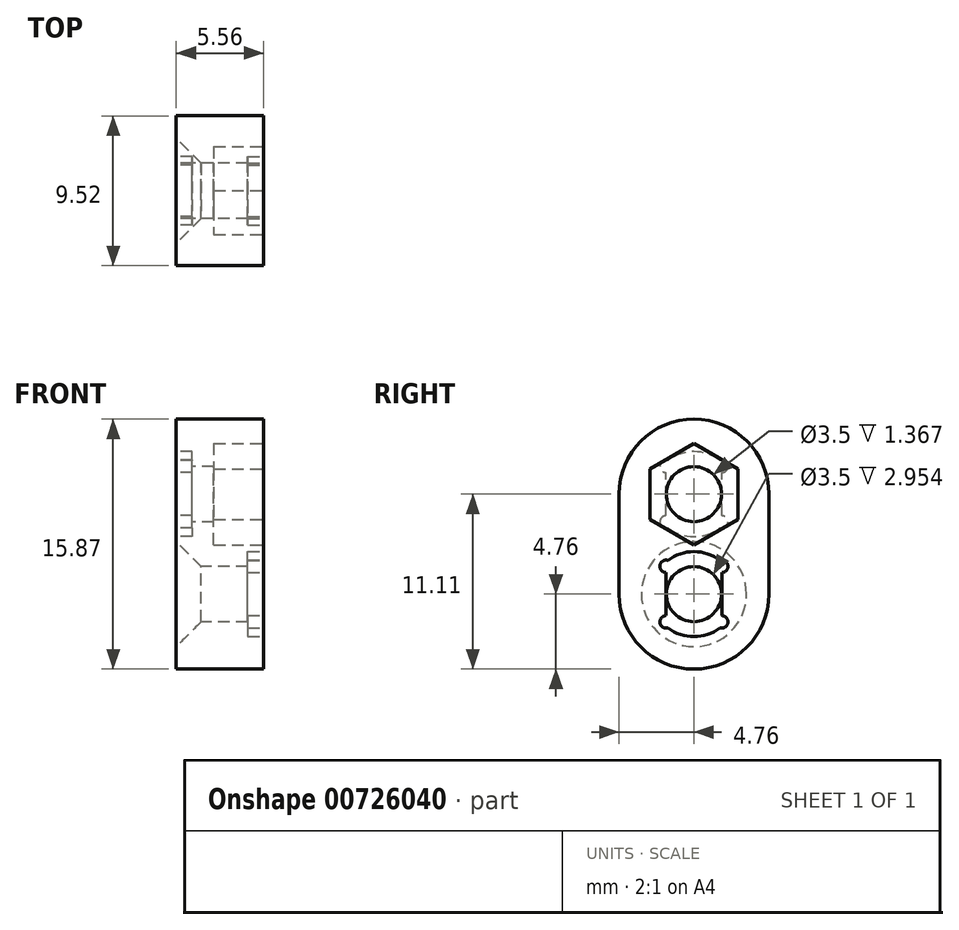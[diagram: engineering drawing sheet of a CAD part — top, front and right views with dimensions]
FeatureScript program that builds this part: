
annotation { "Feature Type Name" : "Feature", "Feature Type Description" : "" }
export const myFeature = defineFeature(function(context is Context, id is Id, definition is map)
    precondition{}
    {
        {
            var Q0;
            Q0=qCreatedBy(makeId("Right.planeOp"),FACE);
            var sketch = newSketch(context, id + "F0", { "sketchPlane" : qUnion([Q0])});
            skCircle(sketch, "E0", {"center": v(0, 0) * mm, "radius": 4.76 * mm});
            skCircle(sketch, "E1", {"center": v(0, 0) * mm, "radius": 1.75 * mm});
            skCircle(sketch, "E2", {"center": v(0, -6.35) * mm, "radius": 4.76 * mm});
            skCircle(sketch, "E3", {"center": v(0, -6.35) * mm, "radius": 1.75 * mm});
            skLineSegment(sketch, "E4", {"start": v(-4.76, 0) * mm, "end": v(-4.76, -6.35) * mm});
            skLineSegment(sketch, "E5", {"start": v(4.76, 0) * mm, "end": v(4.76, -6.35) * mm});
            skSolve(sketch);
        }
        {
            var Q0;
            Q0=makeQuery(id+"F0.imprint","IMPRINT",FACE,{"disambiguationData":[TD([[makeQuery(id+"F0.imprint","IMPRINT",EDGE,{"derivedFrom":sQuery(id+"F0.wireOp",EDGE,"E1")}),-1.0]])]});
            var Q1;
            {var subQ0=sQuery(id+"F0.wireOp",EDGE,"E5");Q1=makeQuery(id+"F0.imprint","IMPRINT",FACE,{"disambiguationData":[TD([[makeQuery(id+"F0.imprint","IMPRINT",EDGE,{"derivedFrom":subQ0}),-1.0]])]});}
            var Q2;
            {var subQ0=sQuery(id+"F0.wireOp",EDGE,"E2");var subQ1=sQuery(id+"F0.wireOp",EDGE,"E0");var subQ2=makeQuery(id+"F0.imprint","INTERSECT",VERTEX,{"disambiguationData":[OD(0.0)],"derivedFrom":[subQ1,subQ0]});Q2=makeQuery(id+"F0.imprint","IMPRINT",FACE,{"disambiguationData":[TD([[makeQuery(id+"F0.imprint","IMPRINT",EDGE,{"disambiguationData":[TD([[subQ2,-1.0]])],"derivedFrom":subQ1}),1.0]])]});}
            var Q3;
            Q3=makeQuery(id+"F0.imprint","IMPRINT",FACE,{"disambiguationData":[TD([[makeQuery(id+"F0.imprint","IMPRINT",EDGE,{"derivedFrom":sQuery(id+"F0.wireOp",EDGE,"E3")}),-1.0]])]});
            var Q4;
            {var subQ0=sQuery(id+"F0.wireOp",EDGE,"E4");Q4=makeQuery(id+"F0.imprint","IMPRINT",FACE,{"disambiguationData":[TD([[makeQuery(id+"F0.imprint","IMPRINT",EDGE,{"derivedFrom":subQ0}),1.0]])]});}
            extrude(context, id + "F1", {"entities" : qUnion([Q0, Q1, Q2, Q3, Q4]), "depth" : 5.56 * mm, "offsetDistance" : 25.4 * mm});
        }
        {
            var Q0;
            Q0=makeQuery(id+"F1.opExtrude","CAP_FACE",FACE,{"disambiguationData":[OSD([sQuery(id+"F0.wireOp",EDGE,"E0"),sQuery(id+"F0.wireOp",EDGE,"E1"),sQuery(id+"F0.wireOp",EDGE,"E2"),sQuery(id+"F0.wireOp",EDGE,"E3"),sQuery(id+"F0.wireOp",EDGE,"E4"),sQuery(id+"F0.wireOp",EDGE,"E5")])],"isStart":false});
            var sketch = newSketch(context, id + "F2", { "sketchPlane" : qUnion([Q0])});
            skLineSegment(sketch, "E6.bottom", {"start": v(-1.77, -8.12) * mm, "end": v(1.77, -8.12) * mm});
            skLineSegment(sketch, "E6.top", {"start": v(-1.77, -4.58) * mm, "end": v(1.77, -4.58) * mm});
            skLineSegment(sketch, "E6.left", {"start": v(-1.77, -8.12) * mm, "end": v(-1.77, -4.58) * mm});
            skLineSegment(sketch, "E6.right", {"start": v(1.77, -8.12) * mm, "end": v(1.77, -4.58) * mm});
            skPoint(sketch, "E6.middle", {"position": v(0, -6.35) * mm});
            skCircle(sketch, "E7", {"center": v(1.77, -4.58) * mm, "radius": 0.4 * mm});
            skCircle(sketch, "E8", {"center": v(-1.77, -4.58) * mm, "radius": 0.4 * mm});
            skCircle(sketch, "E9", {"center": v(-1.77, -8.12) * mm, "radius": 0.4 * mm});
            skCircle(sketch, "E10", {"center": v(1.77, -8.12) * mm, "radius": 0.4 * mm});
            skCircle(sketch, "E11.cCircle", {"center": v(0, 0) * mm, "radius": 3.23 * mm, "construction": true});
            skLineSegment(sketch, "E11.0", {"start": v(0, -3.23) * mm, "end": v(-2.8, -1.61) * mm});
            skLineSegment(sketch, "E11.1", {"start": v(-2.8, -1.61) * mm, "end": v(-2.8, 1.61) * mm});
            skLineSegment(sketch, "E11.2", {"start": v(-2.8, 1.61) * mm, "end": v(0, 3.23) * mm});
            skLineSegment(sketch, "E11.3", {"start": v(0, 3.23) * mm, "end": v(2.8, 1.61) * mm});
            skLineSegment(sketch, "E11.4", {"start": v(2.8, 1.61) * mm, "end": v(2.8, -1.61) * mm});
            skLineSegment(sketch, "E11.5", {"start": v(2.8, -1.61) * mm, "end": v(0, -3.23) * mm});
            skCircle(sketch, "E12", {"center": v(0, -6.35) * mm, "radius": 2.7 * mm});
            skSolve(sketch);
        }
        {
            var Q0;
            {var subQ0=sQuery(id+"F2.wireOp",EDGE,"E6.right");var subQ1=sQuery(id+"F2.wireOp",EDGE,"E6.top");var subQ2=makeQuery(id+"F2.imprint","INTERSECT",VERTEX,{"derivedFrom":[subQ1,subQ0]});Q0=makeQuery(id+"F2.imprint","IMPRINT",FACE,{"disambiguationData":[TD([[makeQuery(id+"F2.imprint","IMPRINT",EDGE,{"disambiguationData":[TD([[subQ2,1.0]])],"derivedFrom":subQ1}),-1.0]])]});}
            var Q1;
            {var subQ0=sQuery(id+"F2.wireOp",EDGE,"E6.right");var subQ1=sQuery(id+"F2.wireOp",EDGE,"E6.top");var subQ2=makeQuery(id+"F2.imprint","INTERSECT",VERTEX,{"derivedFrom":[subQ1,subQ0]});Q1=makeQuery(id+"F2.imprint","IMPRINT",FACE,{"disambiguationData":[TD([[makeQuery(id+"F2.imprint","IMPRINT",EDGE,{"disambiguationData":[TD([[subQ2,1.0]])],"derivedFrom":subQ1}),1.0]])]});}
            var Q2;
            {var subQ0=sQuery(id+"F2.wireOp",EDGE,"E6.right");var subQ1=sQuery(id+"F2.wireOp",EDGE,"E6.bottom");var subQ2=makeQuery(id+"F2.imprint","INTERSECT",VERTEX,{"derivedFrom":[subQ1,subQ0]});Q2=makeQuery(id+"F2.imprint","IMPRINT",FACE,{"disambiguationData":[TD([[makeQuery(id+"F2.imprint","IMPRINT",EDGE,{"disambiguationData":[TD([[subQ2,1.0]])],"derivedFrom":subQ1}),1.0]])]});}
            var Q3;
            {var subQ0=sQuery(id+"F2.wireOp",EDGE,"E6.right");var subQ1=sQuery(id+"F2.wireOp",EDGE,"E6.bottom");var subQ2=makeQuery(id+"F2.imprint","INTERSECT",VERTEX,{"derivedFrom":[subQ1,subQ0]});Q3=makeQuery(id+"F2.imprint","IMPRINT",FACE,{"disambiguationData":[TD([[makeQuery(id+"F2.imprint","IMPRINT",EDGE,{"disambiguationData":[TD([[subQ2,1.0]])],"derivedFrom":subQ1}),-1.0]])]});}
            var Q4;
            {var subQ0=sQuery(id+"F2.wireOp",EDGE,"E6.left");var subQ1=sQuery(id+"F2.wireOp",EDGE,"E6.bottom");var subQ2=makeQuery(id+"F2.imprint","INTERSECT",VERTEX,{"derivedFrom":[subQ1,subQ0]});Q4=makeQuery(id+"F2.imprint","IMPRINT",FACE,{"disambiguationData":[TD([[makeQuery(id+"F2.imprint","IMPRINT",EDGE,{"disambiguationData":[TD([[subQ2,-1.0]])],"derivedFrom":subQ1}),-1.0]])]});}
            var Q5;
            {var subQ0=sQuery(id+"F2.wireOp",EDGE,"E6.left");var subQ1=sQuery(id+"F2.wireOp",EDGE,"E6.bottom");var subQ2=makeQuery(id+"F2.imprint","INTERSECT",VERTEX,{"derivedFrom":[subQ1,subQ0]});Q5=makeQuery(id+"F2.imprint","IMPRINT",FACE,{"disambiguationData":[TD([[makeQuery(id+"F2.imprint","IMPRINT",EDGE,{"disambiguationData":[TD([[subQ2,-1.0]])],"derivedFrom":subQ1}),1.0]])]});}
            var Q6;
            {var subQ0=sQuery(id+"F2.wireOp",EDGE,"E6.left");var subQ1=sQuery(id+"F2.wireOp",EDGE,"E6.top");var subQ2=makeQuery(id+"F2.imprint","INTERSECT",VERTEX,{"derivedFrom":[subQ1,subQ0]});Q6=makeQuery(id+"F2.imprint","IMPRINT",FACE,{"disambiguationData":[TD([[makeQuery(id+"F2.imprint","IMPRINT",EDGE,{"disambiguationData":[TD([[subQ2,-1.0]])],"derivedFrom":subQ1}),-1.0]])]});}
            var Q7;
            {var subQ0=sQuery(id+"F2.wireOp",EDGE,"E6.left");var subQ1=sQuery(id+"F2.wireOp",EDGE,"E6.top");var subQ2=makeQuery(id+"F2.imprint","INTERSECT",VERTEX,{"derivedFrom":[subQ1,subQ0]});Q7=makeQuery(id+"F2.imprint","IMPRINT",FACE,{"disambiguationData":[TD([[makeQuery(id+"F2.imprint","IMPRINT",EDGE,{"disambiguationData":[TD([[subQ2,-1.0]])],"derivedFrom":subQ1}),1.0]])]});}
            var Q8;
            {var subQ1=sQuery(id+"F2.wireOp",EDGE,"E6.top");var subQ7=sQuery(id+"F2.wireOp",EDGE,"E8");var subQ11=makeQuery(id+"F2.imprint","INTERSECT",VERTEX,{"derivedFrom":[subQ1,subQ7]});Q8=makeQuery(id+"F2.imprint","IMPRINT",FACE,{"disambiguationData":[TD([[makeQuery(id+"F2.imprint","IMPRINT",EDGE,{"disambiguationData":[TD([[subQ11,-1.0]])],"derivedFrom":subQ1}),-1.0]])]});}
            var Q9;
            {var subQ0=sQuery(id+"F2.wireOp",EDGE,"E9");var subQ1=sQuery(id+"F2.wireOp",EDGE,"E6.bottom");var subQ2=makeQuery(id+"F2.imprint","INTERSECT",VERTEX,{"derivedFrom":[subQ1,subQ0]});Q9=makeQuery(id+"F2.imprint","IMPRINT",FACE,{"disambiguationData":[TD([[makeQuery(id+"F2.imprint","IMPRINT",EDGE,{"disambiguationData":[TD([[subQ2,-1.0]])],"derivedFrom":subQ1}),1.0]])]});}
            var Q10;
            {var subQ0=sQuery(id+"F2.wireOp",EDGE,"E12");var subQ1=sQuery(id+"F2.wireOp",EDGE,"E6.top");var subQ10=makeQuery(id+"F2.imprint","INTERSECT",VERTEX,{"disambiguationData":[OD(0.0)],"derivedFrom":[subQ1,subQ0]});Q10=makeQuery(id+"F2.imprint","IMPRINT",FACE,{"disambiguationData":[TD([[makeQuery(id+"F2.imprint","IMPRINT",EDGE,{"disambiguationData":[TD([[subQ10,-1.0]])],"derivedFrom":subQ1}),-1.0]])]});}
            var Q11;
            {var subQ0=sQuery(id+"F2.wireOp",EDGE,"E12");var subQ1=sQuery(id+"F2.wireOp",EDGE,"E6.top");var subQ2=makeQuery(id+"F2.imprint","INTERSECT",VERTEX,{"disambiguationData":[OD(1.0)],"derivedFrom":[subQ1,subQ0]});Q11=makeQuery(id+"F2.imprint","IMPRINT",FACE,{"disambiguationData":[TD([[makeQuery(id+"F2.imprint","IMPRINT",EDGE,{"disambiguationData":[TD([[subQ2,-1.0]])],"derivedFrom":subQ1}),-1.0]])]});}
            var Q12;
            {var subQ0=sQuery(id+"F2.wireOp",EDGE,"E12");var subQ7=sQuery(id+"F2.wireOp",EDGE,"E6.bottom");var subQ8=makeQuery(id+"F2.imprint","INTERSECT",VERTEX,{"disambiguationData":[OD(0.0)],"derivedFrom":[subQ7,subQ0]});Q12=makeQuery(id+"F2.imprint","IMPRINT",FACE,{"disambiguationData":[TD([[makeQuery(id+"F2.imprint","IMPRINT",EDGE,{"disambiguationData":[TD([[subQ8,-1.0]])],"derivedFrom":subQ7}),1.0]])]});}
            var Q13;
            {var subQ0=sQuery(id+"F2.wireOp",EDGE,"E12");var subQ1=sQuery(id+"F2.wireOp",EDGE,"E6.bottom");var subQ2=makeQuery(id+"F2.imprint","INTERSECT",VERTEX,{"disambiguationData":[OD(1.0)],"derivedFrom":[subQ1,subQ0]});Q13=makeQuery(id+"F2.imprint","IMPRINT",FACE,{"disambiguationData":[TD([[makeQuery(id+"F2.imprint","IMPRINT",EDGE,{"disambiguationData":[TD([[subQ2,-1.0]])],"derivedFrom":subQ1}),1.0]])]});}
            var Q14;
            {var subQ0=sQuery(id+"F2.wireOp",EDGE,"E12");var subQ1=sQuery(id+"F2.wireOp",EDGE,"E6.top");var subQ2=makeQuery(id+"F2.imprint","INTERSECT",VERTEX,{"disambiguationData":[OD(0.0)],"derivedFrom":[subQ1,subQ0]});Q14=makeQuery(id+"F2.imprint","IMPRINT",FACE,{"disambiguationData":[TD([[makeQuery(id+"F2.imprint","IMPRINT",EDGE,{"disambiguationData":[TD([[subQ2,-1.0]])],"derivedFrom":subQ1}),1.0]])]});}
            var Q15;
            {var subQ0=sQuery(id+"F2.wireOp",EDGE,"E12");var subQ1=sQuery(id+"F2.wireOp",EDGE,"E6.bottom");var subQ2=makeQuery(id+"F2.imprint","INTERSECT",VERTEX,{"disambiguationData":[OD(0.0)],"derivedFrom":[subQ1,subQ0]});Q15=makeQuery(id+"F2.imprint","IMPRINT",FACE,{"disambiguationData":[TD([[makeQuery(id+"F2.imprint","IMPRINT",EDGE,{"disambiguationData":[TD([[subQ2,-1.0]])],"derivedFrom":subQ1}),-1.0]])]});}
            var Q16;
            {var subQ0=sQuery(id+"F2.wireOp",EDGE,"E12");var subQ1=sQuery(id+"F2.wireOp",EDGE,"E8");var subQ2=makeQuery(id+"F2.imprint","INTERSECT",VERTEX,{"disambiguationData":[OD(0.0)],"derivedFrom":[subQ1,subQ0]});Q16=makeQuery(id+"F2.imprint","IMPRINT",FACE,{"disambiguationData":[TD([[makeQuery(id+"F2.imprint","IMPRINT",EDGE,{"disambiguationData":[TD([[subQ2,-1.0]])],"derivedFrom":subQ1}),1.0]])]});}
            var Q17;
            {var subQ0=sQuery(id+"F2.wireOp",EDGE,"E12");var subQ1=sQuery(id+"F2.wireOp",EDGE,"E7");var subQ2=makeQuery(id+"F2.imprint","INTERSECT",VERTEX,{"disambiguationData":[OD(0.0)],"derivedFrom":[subQ1,subQ0]});Q17=makeQuery(id+"F2.imprint","IMPRINT",FACE,{"disambiguationData":[TD([[makeQuery(id+"F2.imprint","IMPRINT",EDGE,{"disambiguationData":[TD([[subQ2,1.0]])],"derivedFrom":subQ1}),1.0]])]});}
            var Q18;
            {var subQ0=sQuery(id+"F2.wireOp",EDGE,"E12");var subQ1=sQuery(id+"F2.wireOp",EDGE,"E10");var subQ2=makeQuery(id+"F2.imprint","INTERSECT",VERTEX,{"disambiguationData":[OD(0.0)],"derivedFrom":[subQ1,subQ0]});Q18=makeQuery(id+"F2.imprint","IMPRINT",FACE,{"disambiguationData":[TD([[makeQuery(id+"F2.imprint","IMPRINT",EDGE,{"disambiguationData":[TD([[subQ2,1.0]])],"derivedFrom":subQ1}),1.0]])]});}
            var Q19;
            {var subQ0=sQuery(id+"F2.wireOp",EDGE,"E12");var subQ1=sQuery(id+"F2.wireOp",EDGE,"E9");var subQ2=makeQuery(id+"F2.imprint","INTERSECT",VERTEX,{"disambiguationData":[OD(0.0)],"derivedFrom":[subQ1,subQ0]});Q19=makeQuery(id+"F2.imprint","IMPRINT",FACE,{"disambiguationData":[TD([[makeQuery(id+"F2.imprint","IMPRINT",EDGE,{"disambiguationData":[TD([[subQ2,-1.0]])],"derivedFrom":subQ1}),1.0]])]});}
            var Q20;
            {var subQ0=sQuery(id+"F2.wireOp",EDGE,"E8");var subQ1=sQuery(id+"F2.wireOp",EDGE,"E6.top");var subQ2=makeQuery(id+"F2.imprint","INTERSECT",VERTEX,{"derivedFrom":[subQ1,subQ0]});Q20=makeQuery(id+"F2.imprint","IMPRINT",FACE,{"disambiguationData":[TD([[makeQuery(id+"F2.imprint","IMPRINT",EDGE,{"disambiguationData":[TD([[subQ2,-1.0]])],"derivedFrom":subQ1}),1.0]])]});}
            var Q21;
            {var subQ0=sQuery(id+"F2.wireOp",EDGE,"E9");var subQ1=sQuery(id+"F2.wireOp",EDGE,"E6.bottom");var subQ2=makeQuery(id+"F2.imprint","INTERSECT",VERTEX,{"derivedFrom":[subQ1,subQ0]});Q21=makeQuery(id+"F2.imprint","IMPRINT",FACE,{"disambiguationData":[TD([[makeQuery(id+"F2.imprint","IMPRINT",EDGE,{"disambiguationData":[TD([[subQ2,-1.0]])],"derivedFrom":subQ1}),-1.0]])]});}
            extrude(context, id + "F3", {"entities" : qUnion([Q0, Q1, Q2, Q3, Q4, Q5, Q6, Q7, Q8, Q9, Q10, Q11, Q12, Q13, Q14, Q15, Q16, Q17, Q18, Q19, Q20, Q21]), "operationType" : NewBodyOperationType.REMOVE, "oppositeDirection" : true, "depth" : 1.02 * mm, "offsetDistance" : 25.4 * mm});
        }
        {
            var Q0;
            Q0=makeQuery(id+"F1.opExtrude","CAP_FACE",FACE,{"disambiguationData":[OSD([sQuery(id+"F0.wireOp",EDGE,"E0"),sQuery(id+"F0.wireOp",EDGE,"E1"),sQuery(id+"F0.wireOp",EDGE,"E2"),sQuery(id+"F0.wireOp",EDGE,"E3"),sQuery(id+"F0.wireOp",EDGE,"E4"),sQuery(id+"F0.wireOp",EDGE,"E5")])],"isStart":true});
            var sketch = newSketch(context, id + "F4", { "sketchPlane" : qUnion([Q0])});
            skLineSegment(sketch, "E13.bottom", {"start": v(-1.77, -1.77) * mm, "end": v(1.77, -1.77) * mm});
            skLineSegment(sketch, "E13.top", {"start": v(-1.77, 1.77) * mm, "end": v(1.77, 1.77) * mm});
            skLineSegment(sketch, "E13.left", {"start": v(-1.77, -1.77) * mm, "end": v(-1.77, 1.77) * mm});
            skLineSegment(sketch, "E13.right", {"start": v(1.77, -1.77) * mm, "end": v(1.77, 1.77) * mm});
            skPoint(sketch, "E13.middle", {"position": v(0, 0) * mm});
            skCircle(sketch, "E14", {"center": v(1.77, 1.77) * mm, "radius": 0.4 * mm});
            skCircle(sketch, "E15", {"center": v(-1.77, 1.77) * mm, "radius": 0.4 * mm});
            skCircle(sketch, "E16", {"center": v(-1.77, -1.77) * mm, "radius": 0.4 * mm});
            skCircle(sketch, "E17", {"center": v(1.77, -1.77) * mm, "radius": 0.4 * mm});
            skCircle(sketch, "E18.cCircle", {"center": v(0, -6.35) * mm, "radius": 3.23 * mm, "construction": true});
            skLineSegment(sketch, "E18.0", {"start": v(0, -9.58) * mm, "end": v(-2.8, -7.96) * mm});
            skLineSegment(sketch, "E18.1", {"start": v(-2.8, -7.96) * mm, "end": v(-2.8, -4.74) * mm});
            skLineSegment(sketch, "E18.2", {"start": v(-2.8, -4.74) * mm, "end": v(0, -3.12) * mm});
            skLineSegment(sketch, "E18.3", {"start": v(0, -3.12) * mm, "end": v(2.8, -4.74) * mm});
            skLineSegment(sketch, "E18.4", {"start": v(2.8, -4.74) * mm, "end": v(2.8, -7.96) * mm});
            skLineSegment(sketch, "E18.5", {"start": v(2.8, -7.96) * mm, "end": v(0, -9.58) * mm});
            skCircle(sketch, "E19", {"center": v(0, 0) * mm, "radius": 2.7 * mm});
            skSolve(sketch);
        }
        {
            var Q0;
            {var subQ0=sQuery(id+"F4.wireOp",EDGE,"E13.right");var subQ1=sQuery(id+"F4.wireOp",EDGE,"E13.bottom");var subQ2=makeQuery(id+"F4.imprint","INTERSECT",VERTEX,{"derivedFrom":[subQ1,subQ0]});Q0=makeQuery(id+"F4.imprint","IMPRINT",FACE,{"disambiguationData":[TD([[makeQuery(id+"F4.imprint","IMPRINT",EDGE,{"disambiguationData":[TD([[subQ2,1.0]])],"derivedFrom":subQ1}),1.0]])]});}
            var Q1;
            {var subQ0=sQuery(id+"F4.wireOp",EDGE,"E13.right");var subQ1=sQuery(id+"F4.wireOp",EDGE,"E13.bottom");var subQ2=makeQuery(id+"F4.imprint","INTERSECT",VERTEX,{"derivedFrom":[subQ1,subQ0]});Q1=makeQuery(id+"F4.imprint","IMPRINT",FACE,{"disambiguationData":[TD([[makeQuery(id+"F4.imprint","IMPRINT",EDGE,{"disambiguationData":[TD([[subQ2,1.0]])],"derivedFrom":subQ1}),-1.0]])]});}
            var Q2;
            {var subQ0=sQuery(id+"F4.wireOp",EDGE,"E13.left");var subQ1=sQuery(id+"F4.wireOp",EDGE,"E13.bottom");var subQ2=makeQuery(id+"F4.imprint","INTERSECT",VERTEX,{"derivedFrom":[subQ1,subQ0]});Q2=makeQuery(id+"F4.imprint","IMPRINT",FACE,{"disambiguationData":[TD([[makeQuery(id+"F4.imprint","IMPRINT",EDGE,{"disambiguationData":[TD([[subQ2,-1.0]])],"derivedFrom":subQ1}),1.0]])]});}
            var Q3;
            {var subQ0=sQuery(id+"F4.wireOp",EDGE,"E13.left");var subQ1=sQuery(id+"F4.wireOp",EDGE,"E13.bottom");var subQ2=makeQuery(id+"F4.imprint","INTERSECT",VERTEX,{"derivedFrom":[subQ1,subQ0]});Q3=makeQuery(id+"F4.imprint","IMPRINT",FACE,{"disambiguationData":[TD([[makeQuery(id+"F4.imprint","IMPRINT",EDGE,{"disambiguationData":[TD([[subQ2,-1.0]])],"derivedFrom":subQ1}),-1.0]])]});}
            var Q4;
            {var subQ0=sQuery(id+"F4.wireOp",EDGE,"E13.left");var subQ1=sQuery(id+"F4.wireOp",EDGE,"E13.top");var subQ2=makeQuery(id+"F4.imprint","INTERSECT",VERTEX,{"derivedFrom":[subQ1,subQ0]});Q4=makeQuery(id+"F4.imprint","IMPRINT",FACE,{"disambiguationData":[TD([[makeQuery(id+"F4.imprint","IMPRINT",EDGE,{"disambiguationData":[TD([[subQ2,-1.0]])],"derivedFrom":subQ1}),-1.0]])]});}
            var Q5;
            {var subQ0=sQuery(id+"F4.wireOp",EDGE,"E13.left");var subQ1=sQuery(id+"F4.wireOp",EDGE,"E13.top");var subQ2=makeQuery(id+"F4.imprint","INTERSECT",VERTEX,{"derivedFrom":[subQ1,subQ0]});Q5=makeQuery(id+"F4.imprint","IMPRINT",FACE,{"disambiguationData":[TD([[makeQuery(id+"F4.imprint","IMPRINT",EDGE,{"disambiguationData":[TD([[subQ2,-1.0]])],"derivedFrom":subQ1}),1.0]])]});}
            var Q6;
            {var subQ0=sQuery(id+"F4.wireOp",EDGE,"E13.right");var subQ1=sQuery(id+"F4.wireOp",EDGE,"E13.top");var subQ2=makeQuery(id+"F4.imprint","INTERSECT",VERTEX,{"derivedFrom":[subQ1,subQ0]});Q6=makeQuery(id+"F4.imprint","IMPRINT",FACE,{"disambiguationData":[TD([[makeQuery(id+"F4.imprint","IMPRINT",EDGE,{"disambiguationData":[TD([[subQ2,1.0]])],"derivedFrom":subQ1}),-1.0]])]});}
            var Q7;
            {var subQ0=sQuery(id+"F4.wireOp",EDGE,"E13.right");var subQ1=sQuery(id+"F4.wireOp",EDGE,"E13.top");var subQ2=makeQuery(id+"F4.imprint","INTERSECT",VERTEX,{"derivedFrom":[subQ1,subQ0]});Q7=makeQuery(id+"F4.imprint","IMPRINT",FACE,{"disambiguationData":[TD([[makeQuery(id+"F4.imprint","IMPRINT",EDGE,{"disambiguationData":[TD([[subQ2,1.0]])],"derivedFrom":subQ1}),1.0]])]});}
            var Q8;
            {var subQ0=sQuery(id+"F4.wireOp",EDGE,"E13.left");var subQ1=makeQuery(id+"F1.opExtrude","CAP_EDGE",EDGE,{"disambiguationData":[OSD([sQuery(id+"F0.wireOp",EDGE,"E1")])],"isStart":true});var subQ2=makeQuery(id+"F4.imprint","INTERSECT",VERTEX,{"disambiguationData":[OD(0.0)],"derivedFrom":[subQ1,subQ0]});Q8=makeQuery(id+"F4.imprint","IMPRINT",FACE,{"disambiguationData":[TD([[makeQuery(id+"F4.imprint","IMPRINT",EDGE,{"disambiguationData":[TD([[subQ2,-1.0]])],"derivedFrom":subQ0}),-1.0]])]});}
            var Q9;
            {var subQ0=sQuery(id+"F4.wireOp",EDGE,"E16");var subQ1=sQuery(id+"F4.wireOp",EDGE,"E13.bottom");var subQ2=makeQuery(id+"F4.imprint","INTERSECT",VERTEX,{"derivedFrom":[subQ1,subQ0]});Q9=makeQuery(id+"F4.imprint","IMPRINT",FACE,{"disambiguationData":[TD([[makeQuery(id+"F4.imprint","IMPRINT",EDGE,{"disambiguationData":[TD([[subQ2,-1.0]])],"derivedFrom":subQ1}),1.0]])]});}
            var Q10;
            {var subQ1=sQuery(id+"F4.wireOp",EDGE,"E13.top");var subQ7=sQuery(id+"F4.wireOp",EDGE,"E15");var subQ11=makeQuery(id+"F4.imprint","INTERSECT",VERTEX,{"derivedFrom":[subQ1,subQ7]});Q10=makeQuery(id+"F4.imprint","IMPRINT",FACE,{"disambiguationData":[TD([[makeQuery(id+"F4.imprint","IMPRINT",EDGE,{"disambiguationData":[TD([[subQ11,-1.0]])],"derivedFrom":subQ1}),-1.0]])]});}
            var Q11;
            {var subQ0=sQuery(id+"F4.wireOp",EDGE,"E19");var subQ1=sQuery(id+"F4.wireOp",EDGE,"E13.top");var subQ10=makeQuery(id+"F4.imprint","INTERSECT",VERTEX,{"disambiguationData":[OD(0.0)],"derivedFrom":[subQ1,subQ0]});Q11=makeQuery(id+"F4.imprint","IMPRINT",FACE,{"disambiguationData":[TD([[makeQuery(id+"F4.imprint","IMPRINT",EDGE,{"disambiguationData":[TD([[subQ10,-1.0]])],"derivedFrom":subQ1}),-1.0]])]});}
            var Q12;
            {var subQ0=sQuery(id+"F4.wireOp",EDGE,"E19");var subQ1=sQuery(id+"F4.wireOp",EDGE,"E13.top");var subQ2=makeQuery(id+"F4.imprint","INTERSECT",VERTEX,{"disambiguationData":[OD(1.0)],"derivedFrom":[subQ1,subQ0]});Q12=makeQuery(id+"F4.imprint","IMPRINT",FACE,{"disambiguationData":[TD([[makeQuery(id+"F4.imprint","IMPRINT",EDGE,{"disambiguationData":[TD([[subQ2,-1.0]])],"derivedFrom":subQ1}),-1.0]])]});}
            var Q13;
            {var subQ0=sQuery(id+"F4.wireOp",EDGE,"E19");var subQ7=sQuery(id+"F4.wireOp",EDGE,"E13.bottom");var subQ8=makeQuery(id+"F4.imprint","INTERSECT",VERTEX,{"disambiguationData":[OD(0.0)],"derivedFrom":[subQ7,subQ0]});Q13=makeQuery(id+"F4.imprint","IMPRINT",FACE,{"disambiguationData":[TD([[makeQuery(id+"F4.imprint","IMPRINT",EDGE,{"disambiguationData":[TD([[subQ8,-1.0]])],"derivedFrom":subQ7}),1.0]])]});}
            var Q14;
            {var subQ0=sQuery(id+"F4.wireOp",EDGE,"E19");var subQ1=sQuery(id+"F4.wireOp",EDGE,"E13.bottom");var subQ2=makeQuery(id+"F4.imprint","INTERSECT",VERTEX,{"disambiguationData":[OD(1.0)],"derivedFrom":[subQ1,subQ0]});Q14=makeQuery(id+"F4.imprint","IMPRINT",FACE,{"disambiguationData":[TD([[makeQuery(id+"F4.imprint","IMPRINT",EDGE,{"disambiguationData":[TD([[subQ2,-1.0]])],"derivedFrom":subQ1}),1.0]])]});}
            var Q15;
            {var subQ0=sQuery(id+"F4.wireOp",EDGE,"E19");var subQ1=sQuery(id+"F4.wireOp",EDGE,"E13.top");var subQ2=makeQuery(id+"F4.imprint","INTERSECT",VERTEX,{"disambiguationData":[OD(0.0)],"derivedFrom":[subQ1,subQ0]});Q15=makeQuery(id+"F4.imprint","IMPRINT",FACE,{"disambiguationData":[TD([[makeQuery(id+"F4.imprint","IMPRINT",EDGE,{"disambiguationData":[TD([[subQ2,-1.0]])],"derivedFrom":subQ1}),1.0]])]});}
            var Q16;
            {var subQ0=sQuery(id+"F4.wireOp",EDGE,"E19");var subQ1=sQuery(id+"F4.wireOp",EDGE,"E13.bottom");var subQ2=makeQuery(id+"F4.imprint","INTERSECT",VERTEX,{"disambiguationData":[OD(0.0)],"derivedFrom":[subQ1,subQ0]});Q16=makeQuery(id+"F4.imprint","IMPRINT",FACE,{"disambiguationData":[TD([[makeQuery(id+"F4.imprint","IMPRINT",EDGE,{"disambiguationData":[TD([[subQ2,-1.0]])],"derivedFrom":subQ1}),-1.0]])]});}
            var Q17;
            {var subQ0=sQuery(id+"F4.wireOp",EDGE,"E19");var subQ1=sQuery(id+"F4.wireOp",EDGE,"E15");var subQ2=makeQuery(id+"F4.imprint","INTERSECT",VERTEX,{"disambiguationData":[OD(0.0)],"derivedFrom":[subQ1,subQ0]});Q17=makeQuery(id+"F4.imprint","IMPRINT",FACE,{"disambiguationData":[TD([[makeQuery(id+"F4.imprint","IMPRINT",EDGE,{"disambiguationData":[TD([[subQ2,-1.0]])],"derivedFrom":subQ1}),1.0]])]});}
            var Q18;
            {var subQ0=sQuery(id+"F4.wireOp",EDGE,"E19");var subQ1=sQuery(id+"F4.wireOp",EDGE,"E16");var subQ2=makeQuery(id+"F4.imprint","INTERSECT",VERTEX,{"disambiguationData":[OD(0.0)],"derivedFrom":[subQ1,subQ0]});Q18=makeQuery(id+"F4.imprint","IMPRINT",FACE,{"disambiguationData":[TD([[makeQuery(id+"F4.imprint","IMPRINT",EDGE,{"disambiguationData":[TD([[subQ2,-1.0]])],"derivedFrom":subQ1}),1.0]])]});}
            var Q19;
            {var subQ0=sQuery(id+"F4.wireOp",EDGE,"E19");var subQ1=sQuery(id+"F4.wireOp",EDGE,"E17");var subQ2=makeQuery(id+"F4.imprint","INTERSECT",VERTEX,{"disambiguationData":[OD(0.0)],"derivedFrom":[subQ1,subQ0]});Q19=makeQuery(id+"F4.imprint","IMPRINT",FACE,{"disambiguationData":[TD([[makeQuery(id+"F4.imprint","IMPRINT",EDGE,{"disambiguationData":[TD([[subQ2,1.0]])],"derivedFrom":subQ1}),1.0]])]});}
            var Q20;
            {var subQ0=sQuery(id+"F4.wireOp",EDGE,"E19");var subQ1=sQuery(id+"F4.wireOp",EDGE,"E14");var subQ2=makeQuery(id+"F4.imprint","INTERSECT",VERTEX,{"disambiguationData":[OD(0.0)],"derivedFrom":[subQ1,subQ0]});Q20=makeQuery(id+"F4.imprint","IMPRINT",FACE,{"disambiguationData":[TD([[makeQuery(id+"F4.imprint","IMPRINT",EDGE,{"disambiguationData":[TD([[subQ2,1.0]])],"derivedFrom":subQ1}),1.0]])]});}
            var Q21;
            {var subQ0=sQuery(id+"F4.wireOp",EDGE,"E15");var subQ1=sQuery(id+"F4.wireOp",EDGE,"E13.top");var subQ2=makeQuery(id+"F4.imprint","INTERSECT",VERTEX,{"derivedFrom":[subQ1,subQ0]});Q21=makeQuery(id+"F4.imprint","IMPRINT",FACE,{"disambiguationData":[TD([[makeQuery(id+"F4.imprint","IMPRINT",EDGE,{"disambiguationData":[TD([[subQ2,-1.0]])],"derivedFrom":subQ1}),1.0]])]});}
            var Q22;
            {var subQ0=sQuery(id+"F4.wireOp",EDGE,"E16");var subQ1=sQuery(id+"F4.wireOp",EDGE,"E13.bottom");var subQ2=makeQuery(id+"F4.imprint","INTERSECT",VERTEX,{"derivedFrom":[subQ1,subQ0]});Q22=makeQuery(id+"F4.imprint","IMPRINT",FACE,{"disambiguationData":[TD([[makeQuery(id+"F4.imprint","IMPRINT",EDGE,{"disambiguationData":[TD([[subQ2,-1.0]])],"derivedFrom":subQ1}),-1.0]])]});}
            extrude(context, id + "F5", {"entities" : qUnion([Q0, Q1, Q2, Q3, Q4, Q5, Q6, Q7, Q8, Q9, Q10, Q11, Q12, Q13, Q14, Q15, Q16, Q17, Q18, Q19, Q20, Q21, Q22]), "operationType" : NewBodyOperationType.REMOVE, "oppositeDirection" : true, "depth" : 1.02 * mm, "offsetDistance" : 25.4 * mm});
        }
        {
            var Q0;
            Q0=makeQuery(id+"F2.imprint","IMPRINT",FACE,{"disambiguationData":[TD([[makeQuery(id+"F2.imprint","IMPRINT",EDGE,{"derivedFrom":sQuery(id+"F2.wireOp",EDGE,"E11.0")}),-1.0]])]});
            extrude(context, id + "F6", {"entities" : qUnion([Q0]), "operationType" : NewBodyOperationType.REMOVE, "oppositeDirection" : true, "depth" : 3.17 * mm, "offsetDistance" : 25.4 * mm});
        }
        {
            var Q0;
            Q0=makeQuery(id+"F1.opExtrude","CAP_EDGE",EDGE,{"disambiguationData":[OSD([sQuery(id+"F0.wireOp",EDGE,"E3")])],"isStart":true});
            chamfer(context, id + "F7", {"entities" : qUnion([Q0]), "width" : 1.59 * mm, "tangentPropagation" : true});
        }
    });
